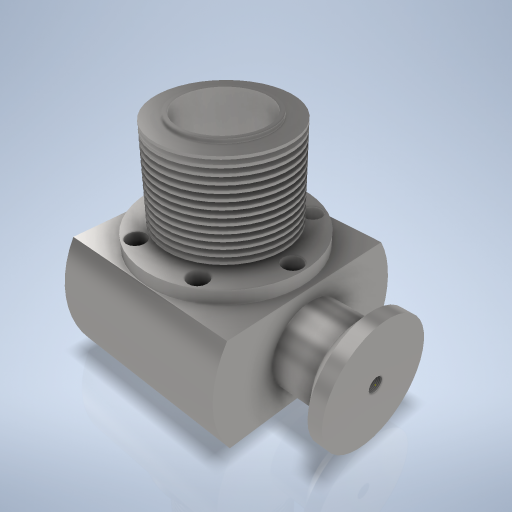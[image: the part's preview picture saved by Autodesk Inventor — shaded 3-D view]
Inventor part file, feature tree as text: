
AUTODESK INVENTOR PART (.ipt)
format: ipt  version: 2024.2 (Build 282272000, 272)  size: 567,808 bytes
history: native  units: mm
features: sketch x12, hole x5, revolve x3, extrude x3, projected_geometry x2, plane x1, pattern_circular x1
ambient origin geometry x8: Origin, YZ Plane, XZ Plane, XY Plane, X Axis, Y Axis, Z Axis, Center Point
bodies: Volumenkörper1 (feature_tree)
feature tree (27):
  revolve  "Umdrehung1"
  extrude  "Extrusion1"  Depth=20.0mm
  extrude  "Extrusion2"  Depth=60.0mm
  plane  "Arbeitsebene1"
  revolve  "Umdrehung2"
  hole  "Bohrung2"  [1 undecoded]
  extrude  "Extrusion3"  Depth=300.0mm
  hole  "Bohrung3"  [1 undecoded]
  hole  "Bohrung4"  [1 undecoded]
  pattern_circular  "Runde Anordnung2"  Count=6 Angle=360.0deg
  revolve  "Umdrehung3"
  sketch  "Skizze16"  dims[d91=20.0mm]
  hole  "Bohrung1"  [1 undecoded]
  hole  "Bohrung5"  [1 undecoded]
  sketch  "Skizze1"  dims[d0=370.0mm d1=20.0mm]
  sketch  "Skizze5"  dims[d2=20.0mm d3=60.0mm]
  sketch  "Skizze6"  dims[d4=270.0mm d5=120.0mm]
  sketch  "Skizze7"  dims[d6=300.0mm d7=177.0mm]
  sketch  "Skizze8"  dims[d8=90.0deg d67=80.0mm]
  projected_geometry  "Projizierte Kontur2"
  sketch  "Skizze9"  dims[d68=80.0mm d69=10.0mm d70=0.0mm]
  sketch  "Skizze10"  dims[d71=215.0mm]
  sketch  "Skizze12"  dims[d72=30.0mm d73=6.0mm d74=4.0mm d75=2.0mm d76=90.0deg d77=60.0mm d78=0.0mm d82=60.0mm d84=360.0deg]
  sketch  "Skizze13"  dims[d86=135.0mm d87=122.5mm]
  sketch  "Skizze15"  dims[d88=170.0mm d89=0.0mm d90=0.0mm]
  projected_geometry  "Projizierte Kontur3"
  sketch  "Skizze17"  dims[d94=10.0mm d95=4.0mm d96=187.5mm d97=252.5mm d98=140.0mm d100=10.0mm d101=10.0mm d103=10.0mm d105=360.0deg d106=22.834936mm d107=50.0mm d108=4.0mm d109=2.0mm d110=90.0deg d111=50.0mm d112=0.0mm d113=22.5mm d114=110.0mm d115=10.0mm d116=0.0mm d117=17.5mm d118=50.0mm d119=4.0mm d120=2.0mm d121=90.0deg d122=115.0mm d123=0.0mm d124=120.0mm d125=30.0deg d126=30.0deg d127=8.376mm d128=20.0mm d129=4.0mm d130=2.0mm d131=90.0deg d132=30.0mm d133=0.0mm d134=60.0mm d135=360.0deg d140=10.0mm d141=140.0mm d142=90.0deg d143=30.0mm d144=6.0mm d145=4.0mm d146=2.0mm d147=90.0deg d148=60.0mm d149=0.0mm]
note: 5 required parameter values undecoded (feature->parameter linkage not recoverable at this tier; creation-order binding heuristic only, values carry confidence <= 0.55)
